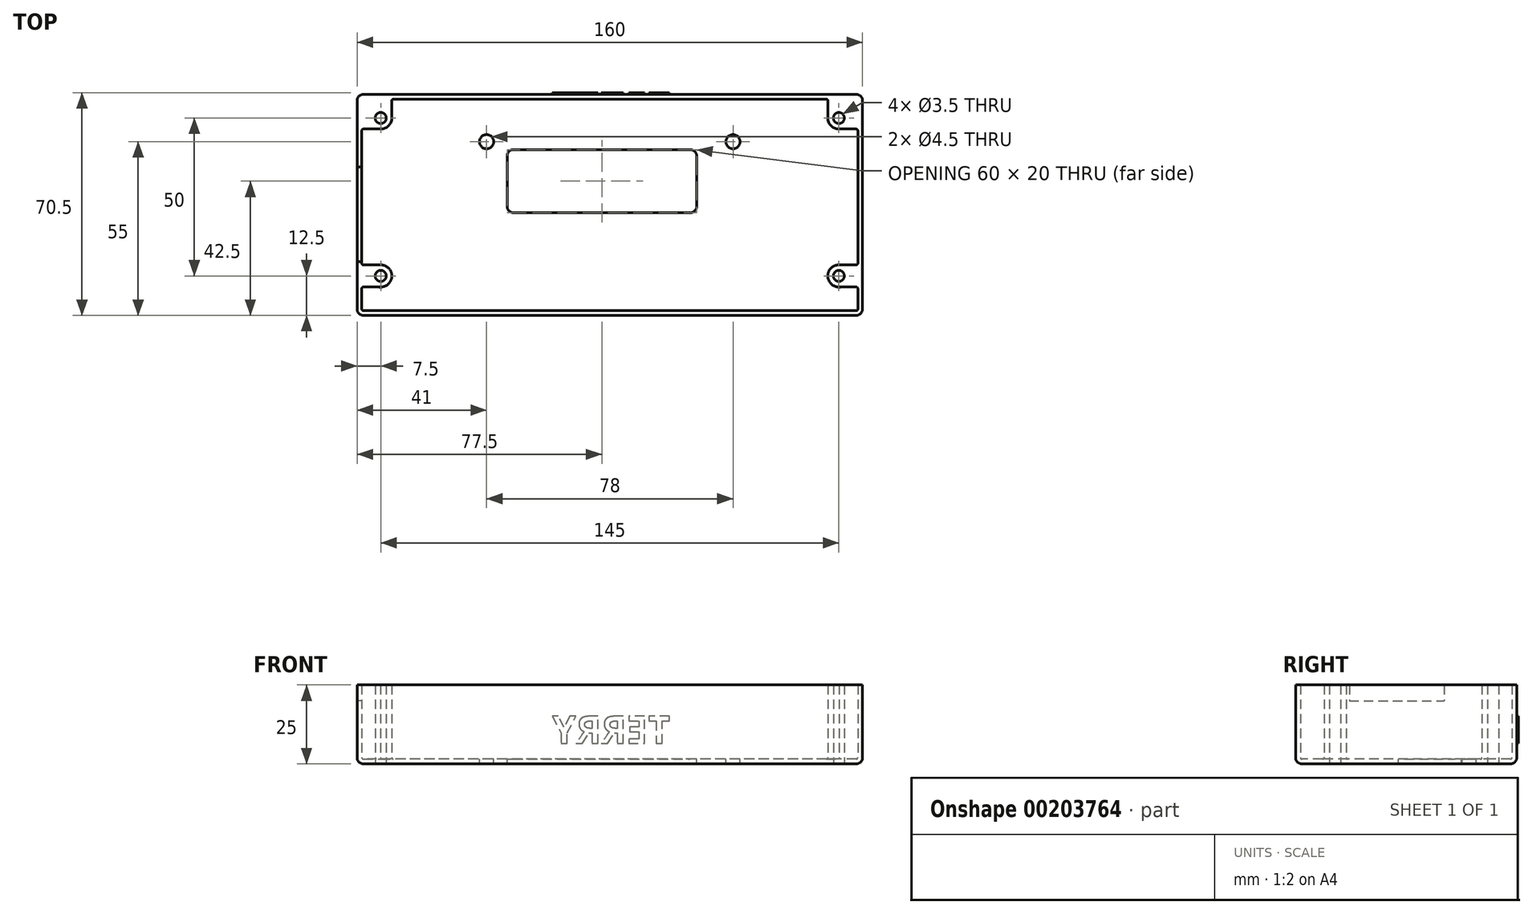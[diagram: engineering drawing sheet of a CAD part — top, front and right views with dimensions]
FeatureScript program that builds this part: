
annotation { "Feature Type Name" : "Feature", "Feature Type Description" : "" }
export const myFeature = defineFeature(function(context is Context, id is Id, definition is map)
    precondition{}
    {
        {
            var Q0;
            Q0=qCreatedBy(makeId("Top.planeOp"),FACE);
            var sketch = newSketch(context, id + "F0", { "sketchPlane" : qUnion([Q0])});
            skLineSegment(sketch, "E0.bottom", {"start": v(80, 35) * mm, "end": v(-80, 35) * mm});
            skLineSegment(sketch, "E0.top", {"start": v(80, -35) * mm, "end": v(-80, -35) * mm});
            skLineSegment(sketch, "E0.left", {"start": v(80, 35) * mm, "end": v(80, -35) * mm});
            skLineSegment(sketch, "E0.right", {"start": v(-80, 35) * mm, "end": v(-80, -35) * mm});
            skPoint(sketch, "E0.middle", {"position": v(0, 0) * mm});
            skLineSegment(sketch, "E1.0", {"start": v(78.5, 33.5) * mm, "end": v(-78.5, 33.5) * mm});
            skLineSegment(sketch, "E2.0", {"start": v(78.5, 33.5) * mm, "end": v(78.5, -33.5) * mm});
            skLineSegment(sketch, "E2.1", {"start": v(78.5, -33.5) * mm, "end": v(-78.5, -33.5) * mm});
            skLineSegment(sketch, "E2.2", {"start": v(-78.5, 33.5) * mm, "end": v(-78.5, -33.5) * mm});
            skSolve(sketch);
        }
        {
            var Q0;
            Q0=makeQuery(id+"F0.imprint","IMPRINT",FACE,{"disambiguationData":[TD([[makeQuery(id+"F0.imprint","IMPRINT",EDGE,{"derivedFrom":sQuery(id+"F0.wireOp",EDGE,"E0.bottom")}),1.0]])]});
            extrude(context, id + "F1", {"entities" : qUnion([Q0]), "depth" : 25 * mm});
        }
        {
            var Q0;
            Q0=qCreatedBy(makeId("Top.planeOp"),FACE);
            var sketch = newSketch(context, id + "F2", { "sketchPlane" : qUnion([Q0])});
            skLineSegment(sketch, "E3.bottom", {"start": v(-80, -35) * mm, "end": v(80, -35) * mm});
            skLineSegment(sketch, "E3.top", {"start": v(-80, 35) * mm, "end": v(80, 35) * mm});
            skLineSegment(sketch, "E3.left", {"start": v(-80, -35) * mm, "end": v(-80, 35) * mm});
            skLineSegment(sketch, "E3.right", {"start": v(80, -35) * mm, "end": v(80, 35) * mm});
            skPoint(sketch, "E3.middle", {"position": v(0, 0) * mm});
            skSolve(sketch);
        }
        {
            var Q0;
            Q0=makeQuery(id+"F2.imprint","IMPRINT",FACE,{"disambiguationData":[TD([[makeQuery(id+"F2.imprint","IMPRINT",EDGE,{"derivedFrom":sQuery(id+"F2.wireOp",EDGE,"E3.bottom")}),1.0]])]});
            extrude(context, id + "F3", {"entities" : qUnion([Q0]), "operationType" : NewBodyOperationType.ADD, "depth" : 1.5 * mm});
        }
        {
            var Q0;
            Q0=qCreatedBy(makeId("Top.planeOp"),FACE);
            var sketch = newSketch(context, id + "F4", { "sketchPlane" : qUnion([Q0])});
            skLineSegment(sketch, "E4", {"start": v(0, 0) * mm, "end": v(0, 27.5) * mm, "construction": true});
            skLineSegment(sketch, "E5", {"start": v(0, 27.5) * mm, "end": v(-72.5, 27.5) * mm, "construction": true});
            skLineSegment(sketch, "E6", {"start": v(-72.5, 27.5) * mm, "end": v(-72.5, -22.5) * mm, "construction": true});
            skLineSegment(sketch, "E7", {"start": v(72.5, -22.5) * mm, "end": v(72.5, 27.5) * mm, "construction": true});
            skArc(sketch, "E8", {"start": v(-72.5, 24) * mm, "mid": v(-70.03, 25.03) * mm, "end": v(-69, 27.5) * mm});
            skArc(sketch, "E9", {"start": v(-72.54, -26) * mm, "mid": v(-69, -22.52) * mm, "end": v(-72.5, -19) * mm});
            skLineSegment(sketch, "E10", {"start": v(0, 27.5) * mm, "end": v(0, 35) * mm, "construction": true});
            skLineSegment(sketch, "E11", {"start": v(0, 35) * mm, "end": v(-80, 35) * mm, "construction": true});
            skLineSegment(sketch, "E12", {"start": v(-80, 35) * mm, "end": v(-80, -35) * mm, "construction": true});
            skLineSegment(sketch, "E13", {"start": v(-69, 27.5) * mm, "end": v(-69, 35) * mm});
            skLineSegment(sketch, "E14", {"start": v(-72.5, 24) * mm, "end": v(-80, 24) * mm});
            skLineSegment(sketch, "E15", {"start": v(-72.5, -19) * mm, "end": v(-80, -19) * mm});
            skLineSegment(sketch, "E16", {"start": v(-72.54, -26) * mm, "end": v(-80, -26) * mm});
            skLineSegment(sketch, "E17.MirrorCS", {"start": v(69, 27.5) * mm, "end": v(69, 35) * mm});
            skArc(sketch, "E18.MirrorCS", {"start": v(72.5, 24) * mm, "mid": v(70.03, 25.03) * mm, "end": v(69, 27.5) * mm});
            skLineSegment(sketch, "E19.MirrorCS", {"start": v(72.5, 24) * mm, "end": v(80, 24) * mm});
            skLineSegment(sketch, "E20.MirrorCS", {"start": v(72.5, -19) * mm, "end": v(80, -19) * mm});
            skArc(sketch, "E21.MirrorCS", {"start": v(72.54, -26) * mm, "mid": v(69, -22.52) * mm, "end": v(72.5, -19) * mm});
            skLineSegment(sketch, "E22.MirrorCS", {"start": v(72.54, -26) * mm, "end": v(80, -26) * mm});
            skLineSegment(sketch, "E23", {"start": v(-80, -19) * mm, "end": v(-80, -26) * mm});
            skLineSegment(sketch, "E24", {"start": v(-80, 24) * mm, "end": v(-80, 35) * mm});
            skLineSegment(sketch, "E25", {"start": v(69, 35) * mm, "end": v(80, 35) * mm});
            skLineSegment(sketch, "E26", {"start": v(80, 24) * mm, "end": v(80, 35) * mm});
            skLineSegment(sketch, "E27", {"start": v(80, -19) * mm, "end": v(80, -26) * mm});
            skLineSegment(sketch, "E28", {"start": v(-80, 35) * mm, "end": v(-69, 35) * mm});
            skCircle(sketch, "E29", {"center": v(-72.5, 27.5) * mm, "radius": 1.75 * mm});
            skCircle(sketch, "E30", {"center": v(72.5, 27.5) * mm, "radius": 1.75 * mm});
            skCircle(sketch, "E31", {"center": v(72.5, -22.5) * mm, "radius": 1.75 * mm});
            skCircle(sketch, "E32", {"center": v(-72.5, -22.5) * mm, "radius": 1.75 * mm});
            skLineSegment(sketch, "E33", {"start": v(-72.5, 27.5) * mm, "end": v(-39, 27.5) * mm, "construction": true});
            skPoint(sketch, "E33.endSnap0", {"position": v(-36.25, 27.5) * mm});
            skLineSegment(sketch, "E34", {"start": v(-39, 27.5) * mm, "end": v(-39, 20) * mm, "construction": true});
            skLineSegment(sketch, "E35", {"start": v(-39, 20) * mm, "end": v(39, 20) * mm, "construction": true});
            skCircle(sketch, "E36", {"center": v(-39, 20) * mm, "radius": 2.25 * mm});
            skCircle(sketch, "E37", {"center": v(39, 20) * mm, "radius": 2.25 * mm});
            skLineSegment(sketch, "E38", {"start": v(-32.5, -2.5) * mm, "end": v(-32.5, 17.5) * mm});
            skLineSegment(sketch, "E39", {"start": v(-32.5, 17.5) * mm, "end": v(27.5, 17.5) * mm});
            skLineSegment(sketch, "E40", {"start": v(27.5, 17.5) * mm, "end": v(27.5, -2.5) * mm});
            skLineSegment(sketch, "E41", {"start": v(27.5, -2.5) * mm, "end": v(-32.5, -2.5) * mm});
            skSolve(sketch);
        }
        {
            var Q0;
            Q0=makeQuery(id+"F4.imprint","IMPRINT",FACE,{"disambiguationData":[TD([[makeQuery(id+"F4.imprint","IMPRINT",EDGE,{"derivedFrom":sQuery(id+"F4.wireOp",EDGE,"E8")}),1.0]])]});
            var Q1;
            Q1=makeQuery(id+"F4.imprint","IMPRINT",FACE,{"disambiguationData":[TD([[makeQuery(id+"F4.imprint","IMPRINT",EDGE,{"derivedFrom":sQuery(id+"F4.wireOp",EDGE,"E9")}),1.0]])]});
            var Q2;
            Q2=makeQuery(id+"F4.imprint","IMPRINT",FACE,{"disambiguationData":[TD([[makeQuery(id+"F4.imprint","IMPRINT",EDGE,{"derivedFrom":sQuery(id+"F4.wireOp",EDGE,"E17.MirrorCS")}),-1.0]])]});
            var Q3;
            Q3=makeQuery(id+"F4.imprint","IMPRINT",FACE,{"disambiguationData":[TD([[makeQuery(id+"F4.imprint","IMPRINT",EDGE,{"derivedFrom":sQuery(id+"F4.wireOp",EDGE,"E20.MirrorCS")}),-1.0]])]});
            var Q4;
            Q4=sQuery(id+"F4.wireOp",EDGE,"E16");
            var Q5;
            Q5=sQuery(id+"F4.wireOp",EDGE,"E15");
            var Q6;
            Q6=sQuery(id+"F4.wireOp",EDGE,"E9");
            var Q7;
            Q7=sQuery(id+"F4.wireOp",EDGE,"E23");
            var Q8;
            Q8=sQuery(id+"F4.wireOp",EDGE,"E21.MirrorCS");
            var Q9;
            Q9=sQuery(id+"F4.wireOp",EDGE,"E27");
            var Q10;
            Q10=sQuery(id+"F4.wireOp",EDGE,"E22.MirrorCS");
            var Q11;
            Q11=sQuery(id+"F4.wireOp",EDGE,"E20.MirrorCS");
            var Q12;
            Q12=sQuery(id+"F4.wireOp",EDGE,"E25");
            var Q13;
            Q13=sQuery(id+"F4.wireOp",EDGE,"E26");
            var Q14;
            Q14=sQuery(id+"F4.wireOp",EDGE,"E19.MirrorCS");
            var Q15;
            Q15=sQuery(id+"F4.wireOp",EDGE,"E17.MirrorCS");
            var Q16;
            Q16=sQuery(id+"F4.wireOp",EDGE,"E18.MirrorCS");
            var Q17;
            Q17=sQuery(id+"F4.wireOp",EDGE,"E14");
            var Q18;
            Q18=sQuery(id+"F4.wireOp",EDGE,"E8");
            var Q19;
            Q19=sQuery(id+"F4.wireOp",EDGE,"E24");
            var Q20;
            Q20=sQuery(id+"F4.wireOp",EDGE,"E13");
            var Q21;
            Q21=sQuery(id+"F4.wireOp",EDGE,"E28");
            extrude(context, id + "F5", {"entities" : qUnion([Q0, Q1, Q2, Q3]), "operationType" : NewBodyOperationType.ADD, "surfaceEntities" : qUnion([Q4, Q5, Q6, Q7, Q8, Q9, Q10, Q11, Q12, Q13, Q14, Q15, Q16, Q17, Q18, Q19, Q20, Q21]), "depth" : 25 * mm});
        }
        {
            var Q0;
            Q0=makeQuery(id+"F5.boolean.opBoolean","SPLIT",FACE,{"disambiguationData":[TD([makeQuery(id+"F5.opExtrude","SWEPT_FACE",FACE,{"disambiguationData":[OSD([sQuery(id+"F4.wireOp",EDGE,"E29")])]})])],"derivedFrom":makeQuery(id+"F3.opExtrude","CAP_FACE",FACE,{"disambiguationData":[OSD([sQuery(id+"F2.wireOp",EDGE,"E3.bottom"),sQuery(id+"F2.wireOp",EDGE,"E3.top"),sQuery(id+"F2.wireOp",EDGE,"E3.left"),sQuery(id+"F2.wireOp",EDGE,"E3.right")])],"isStart":false})});
            var Q1;
            Q1=makeQuery(id+"F5.boolean.opBoolean","SPLIT",FACE,{"disambiguationData":[TD([makeQuery(id+"F5.opExtrude","SWEPT_FACE",FACE,{"disambiguationData":[OSD([sQuery(id+"F4.wireOp",EDGE,"E32")])]})])],"derivedFrom":makeQuery(id+"F3.opExtrude","CAP_FACE",FACE,{"disambiguationData":[OSD([sQuery(id+"F2.wireOp",EDGE,"E3.bottom"),sQuery(id+"F2.wireOp",EDGE,"E3.top"),sQuery(id+"F2.wireOp",EDGE,"E3.left"),sQuery(id+"F2.wireOp",EDGE,"E3.right")])],"isStart":false})});
            var Q2;
            Q2=makeQuery(id+"F5.boolean.opBoolean","SPLIT",FACE,{"disambiguationData":[TD([makeQuery(id+"F5.opExtrude","SWEPT_FACE",FACE,{"disambiguationData":[OSD([sQuery(id+"F4.wireOp",EDGE,"E30")])]})])],"derivedFrom":makeQuery(id+"F3.opExtrude","CAP_FACE",FACE,{"disambiguationData":[OSD([sQuery(id+"F2.wireOp",EDGE,"E3.bottom"),sQuery(id+"F2.wireOp",EDGE,"E3.top"),sQuery(id+"F2.wireOp",EDGE,"E3.left"),sQuery(id+"F2.wireOp",EDGE,"E3.right")])],"isStart":false})});
            var Q3;
            Q3=makeQuery(id+"F5.boolean.opBoolean","SPLIT",FACE,{"disambiguationData":[TD([makeQuery(id+"F5.opExtrude","SWEPT_FACE",FACE,{"disambiguationData":[OSD([sQuery(id+"F4.wireOp",EDGE,"E31")])]})])],"derivedFrom":makeQuery(id+"F3.opExtrude","CAP_FACE",FACE,{"disambiguationData":[OSD([sQuery(id+"F2.wireOp",EDGE,"E3.bottom"),sQuery(id+"F2.wireOp",EDGE,"E3.top"),sQuery(id+"F2.wireOp",EDGE,"E3.left"),sQuery(id+"F2.wireOp",EDGE,"E3.right")])],"isStart":false})});
            extrude(context, id + "F6", {"entities" : qUnion([Q0, Q1, Q2, Q3]), "operationType" : NewBodyOperationType.REMOVE, "endBound" : BoundingType.UP_TO_NEXT, "oppositeDirection" : true, "depth" : 25 * mm});
        }
        {
            var Q0;
            Q0=makeQuery(id+"F5.boolean.opBoolean","SPLIT",FACE,{"disambiguationData":[TD([makeQuery(id+"F1.opExtrude","SWEPT_FACE",FACE,{"disambiguationData":[OSD([sQuery(id+"F0.wireOp",EDGE,"E1.0")])]})])],"derivedFrom":makeQuery(id+"F3.opExtrude","CAP_FACE",FACE,{"disambiguationData":[OSD([sQuery(id+"F2.wireOp",EDGE,"E3.bottom"),sQuery(id+"F2.wireOp",EDGE,"E3.top"),sQuery(id+"F2.wireOp",EDGE,"E3.left"),sQuery(id+"F2.wireOp",EDGE,"E3.right")])],"isStart":false})});
            var sketch = newSketch(context, id + "F7", { "sketchPlane" : qUnion([Q0])});
            skLineSegment(sketch, "E42", {"start": v(-72.5, 27.5) * mm, "end": v(-39, 27.5) * mm, "construction": true});
            skLineSegment(sketch, "E43", {"start": v(-39, 27.5) * mm, "end": v(-39, 20) * mm, "construction": true});
            skLineSegment(sketch, "E44", {"start": v(-39, 20) * mm, "end": v(39, 20) * mm, "construction": true});
            skCircle(sketch, "E45", {"center": v(-39, 20) * mm, "radius": 2.25 * mm});
            skCircle(sketch, "E46", {"center": v(39, 20) * mm, "radius": 2.25 * mm});
            skLineSegment(sketch, "E47.bottom", {"start": v(-32.5, -2.5) * mm, "end": v(27.5, -2.5) * mm});
            skLineSegment(sketch, "E47.top", {"start": v(-32.5, 17.5) * mm, "end": v(27.5, 17.5) * mm});
            skLineSegment(sketch, "E47.left", {"start": v(-32.5, -2.5) * mm, "end": v(-32.5, 17.5) * mm});
            skLineSegment(sketch, "E47.right", {"start": v(27.5, -2.5) * mm, "end": v(27.5, 17.5) * mm});
            skSolve(sketch);
        }
        {
            var Q0;
            Q0=makeQuery(id+"F7.imprint","IMPRINT",FACE,{"disambiguationData":[TD([[makeQuery(id+"F7.imprint","IMPRINT",EDGE,{"derivedFrom":sQuery(id+"F7.wireOp",EDGE,"E47.bottom")}),1.0]])]});
            var Q1;
            Q1=makeQuery(id+"F7.imprint","IMPRINT",FACE,{"disambiguationData":[TD([[makeQuery(id+"F7.imprint","IMPRINT",EDGE,{"derivedFrom":sQuery(id+"F7.wireOp",EDGE,"E45")}),1.0]])]});
            var Q2;
            Q2=makeQuery(id+"F7.imprint","IMPRINT",FACE,{"disambiguationData":[TD([[makeQuery(id+"F7.imprint","IMPRINT",EDGE,{"derivedFrom":sQuery(id+"F7.wireOp",EDGE,"E46")}),1.0]])]});
            extrude(context, id + "F8", {"entities" : qUnion([Q0, Q1, Q2]), "operationType" : NewBodyOperationType.REMOVE, "endBound" : BoundingType.UP_TO_NEXT, "oppositeDirection" : true, "depth" : 25 * mm});
        }
        {
            var Q0;
            Q0=makeQuery(id+"F1.opExtrude","SWEPT_FACE",FACE,{"disambiguationData":[OSD([sQuery(id+"F0.wireOp",EDGE,"E0.right")])]});
            var sketch = newSketch(context, id + "F9", { "sketchPlane" : qUnion([Q0])});
            skLineSegment(sketch, "E48", {"start": v(35, 25) * mm, "end": v(18, 25) * mm});
            skLineSegment(sketch, "E49.bottom", {"start": v(18, 25) * mm, "end": v(-12, 25) * mm});
            skLineSegment(sketch, "E49.top", {"start": v(18, 20) * mm, "end": v(-12, 20) * mm});
            skLineSegment(sketch, "E49.left", {"start": v(18, 25) * mm, "end": v(18, 20) * mm});
            skLineSegment(sketch, "E49.right", {"start": v(-12, 25) * mm, "end": v(-12, 20) * mm});
            skSolve(sketch);
        }
        {
            var Q0;
            Q0=makeQuery(id+"F9.imprint","IMPRINT",FACE,{"disambiguationData":[TD([[makeQuery(id+"F9.imprint","IMPRINT",EDGE,{"derivedFrom":sQuery(id+"F9.wireOp",EDGE,"E49.bottom")}),-1.0]])]});
            extrude(context, id + "F10", {"entities" : qUnion([Q0]), "operationType" : NewBodyOperationType.REMOVE, "endBound" : BoundingType.UP_TO_NEXT, "oppositeDirection" : true, "depth" : 25 * mm});
        }
        {
            var Q0;
            Q0=makeQuery(id+"F3.boolean.opBoolean","INTERSECT",EDGE,{"derivedFrom":[makeQuery(id+"F1.opExtrude","SWEPT_FACE",FACE,{"disambiguationData":[OSD([sQuery(id+"F0.wireOp",EDGE,"E1.0")])]}),makeQuery(id+"F3.opExtrude","CAP_FACE",FACE,{"disambiguationData":[OSD([sQuery(id+"F2.wireOp",EDGE,"E3.bottom"),sQuery(id+"F2.wireOp",EDGE,"E3.top"),sQuery(id+"F2.wireOp",EDGE,"E3.left"),sQuery(id+"F2.wireOp",EDGE,"E3.right")])],"isStart":false})]});
            var Q1;
            Q1=makeQuery(id+"F5.boolean.opBoolean","INTERSECT",EDGE,{"derivedFrom":[makeQuery(id+"F3.opExtrude","CAP_FACE",FACE,{"disambiguationData":[OSD([sQuery(id+"F2.wireOp",EDGE,"E3.bottom"),sQuery(id+"F2.wireOp",EDGE,"E3.top"),sQuery(id+"F2.wireOp",EDGE,"E3.left"),sQuery(id+"F2.wireOp",EDGE,"E3.right")])],"isStart":false}),makeQuery(id+"F5.opExtrude","SWEPT_FACE",FACE,{"disambiguationData":[OSD([sQuery(id+"F4.wireOp",EDGE,"E13")])]})]});
            var Q2;
            Q2=makeQuery(id+"F5.boolean.opBoolean","INTERSECT",EDGE,{"derivedFrom":[makeQuery(id+"F3.opExtrude","CAP_FACE",FACE,{"disambiguationData":[OSD([sQuery(id+"F2.wireOp",EDGE,"E3.bottom"),sQuery(id+"F2.wireOp",EDGE,"E3.top"),sQuery(id+"F2.wireOp",EDGE,"E3.left"),sQuery(id+"F2.wireOp",EDGE,"E3.right")])],"isStart":false}),makeQuery(id+"F5.opExtrude","SWEPT_FACE",FACE,{"disambiguationData":[OSD([sQuery(id+"F4.wireOp",EDGE,"E8")])]})]});
            var Q3;
            Q3=makeQuery(id+"F5.boolean.opBoolean","INTERSECT",EDGE,{"derivedFrom":[makeQuery(id+"F3.opExtrude","CAP_FACE",FACE,{"disambiguationData":[OSD([sQuery(id+"F2.wireOp",EDGE,"E3.bottom"),sQuery(id+"F2.wireOp",EDGE,"E3.top"),sQuery(id+"F2.wireOp",EDGE,"E3.left"),sQuery(id+"F2.wireOp",EDGE,"E3.right")])],"isStart":false}),makeQuery(id+"F5.opExtrude","SWEPT_FACE",FACE,{"disambiguationData":[OSD([sQuery(id+"F4.wireOp",EDGE,"E14")])]})]});
            var Q4;
            {var subQ0=makeQuery(id+"F1.opExtrude","SWEPT_FACE",FACE,{"disambiguationData":[OSD([sQuery(id+"F0.wireOp",EDGE,"E2.2")])]});var subQ1=makeQuery(id+"F3.opExtrude","CAP_FACE",FACE,{"disambiguationData":[OSD([sQuery(id+"F2.wireOp",EDGE,"E3.bottom"),sQuery(id+"F2.wireOp",EDGE,"E3.top"),sQuery(id+"F2.wireOp",EDGE,"E3.left"),sQuery(id+"F2.wireOp",EDGE,"E3.right")])],"isStart":false});Q4=makeQuery(id+"F5.boolean.opBoolean","SPLIT",EDGE,{"disambiguationData":[TD([makeQuery(id+"F5.opExtrude","SWEPT_FACE",FACE,{"disambiguationData":[OSD([sQuery(id+"F4.wireOp",EDGE,"E14")])]})])],"derivedFrom":makeQuery(id+"F3.boolean.opBoolean","INTERSECT",EDGE,{"derivedFrom":[subQ0,subQ1]})});}
            var Q5;
            Q5=makeQuery(id+"F5.boolean.opBoolean","INTERSECT",EDGE,{"derivedFrom":[makeQuery(id+"F3.opExtrude","CAP_FACE",FACE,{"disambiguationData":[OSD([sQuery(id+"F2.wireOp",EDGE,"E3.bottom"),sQuery(id+"F2.wireOp",EDGE,"E3.top"),sQuery(id+"F2.wireOp",EDGE,"E3.left"),sQuery(id+"F2.wireOp",EDGE,"E3.right")])],"isStart":false}),makeQuery(id+"F5.opExtrude","SWEPT_FACE",FACE,{"disambiguationData":[OSD([sQuery(id+"F4.wireOp",EDGE,"E9")])]})]});
            var Q6;
            Q6=makeQuery(id+"F5.boolean.opBoolean","INTERSECT",EDGE,{"derivedFrom":[makeQuery(id+"F3.opExtrude","CAP_FACE",FACE,{"disambiguationData":[OSD([sQuery(id+"F2.wireOp",EDGE,"E3.bottom"),sQuery(id+"F2.wireOp",EDGE,"E3.top"),sQuery(id+"F2.wireOp",EDGE,"E3.left"),sQuery(id+"F2.wireOp",EDGE,"E3.right")])],"isStart":false}),makeQuery(id+"F5.opExtrude","SWEPT_FACE",FACE,{"disambiguationData":[OSD([sQuery(id+"F4.wireOp",EDGE,"E16")])]})]});
            var Q7;
            {var subQ0=makeQuery(id+"F1.opExtrude","SWEPT_FACE",FACE,{"disambiguationData":[OSD([sQuery(id+"F0.wireOp",EDGE,"E2.2")])]});var subQ1=makeQuery(id+"F3.opExtrude","CAP_FACE",FACE,{"disambiguationData":[OSD([sQuery(id+"F2.wireOp",EDGE,"E3.bottom"),sQuery(id+"F2.wireOp",EDGE,"E3.top"),sQuery(id+"F2.wireOp",EDGE,"E3.left"),sQuery(id+"F2.wireOp",EDGE,"E3.right")])],"isStart":false});Q7=makeQuery(id+"F5.boolean.opBoolean","SPLIT",EDGE,{"disambiguationData":[TD([makeQuery(id+"F1.opExtrude","SWEPT_FACE",FACE,{"disambiguationData":[OSD([sQuery(id+"F0.wireOp",EDGE,"E2.1")])]})])],"derivedFrom":makeQuery(id+"F3.boolean.opBoolean","INTERSECT",EDGE,{"derivedFrom":[subQ0,subQ1]})});}
            var Q8;
            Q8=makeQuery(id+"F5.boolean.opBoolean","INTERSECT",EDGE,{"derivedFrom":[makeQuery(id+"F1.opExtrude","SWEPT_FACE",FACE,{"disambiguationData":[OSD([sQuery(id+"F0.wireOp",EDGE,"E2.2")])]}),makeQuery(id+"F5.opExtrude","SWEPT_FACE",FACE,{"disambiguationData":[OSD([sQuery(id+"F4.wireOp",EDGE,"E14")])]})]});
            var Q9;
            Q9=makeQuery(id+"F5.boolean.opBoolean","INTERSECT",EDGE,{"derivedFrom":[makeQuery(id+"F1.opExtrude","SWEPT_FACE",FACE,{"disambiguationData":[OSD([sQuery(id+"F0.wireOp",EDGE,"E1.0")])]}),makeQuery(id+"F5.opExtrude","SWEPT_FACE",FACE,{"disambiguationData":[OSD([sQuery(id+"F4.wireOp",EDGE,"E13")])]})]});
            var Q10;
            Q10=makeQuery(id+"F5.boolean.opBoolean","INTERSECT",EDGE,{"derivedFrom":[makeQuery(id+"F1.opExtrude","SWEPT_FACE",FACE,{"disambiguationData":[OSD([sQuery(id+"F0.wireOp",EDGE,"E2.2")])]}),makeQuery(id+"F5.opExtrude","SWEPT_FACE",FACE,{"disambiguationData":[OSD([sQuery(id+"F4.wireOp",EDGE,"E16")])]})]});
            var Q11;
            Q11=makeQuery(id+"F3.boolean.opBoolean","INTERSECT",EDGE,{"derivedFrom":[makeQuery(id+"F1.opExtrude","SWEPT_FACE",FACE,{"disambiguationData":[OSD([sQuery(id+"F0.wireOp",EDGE,"E2.1")])]}),makeQuery(id+"F3.opExtrude","CAP_FACE",FACE,{"disambiguationData":[OSD([sQuery(id+"F2.wireOp",EDGE,"E3.bottom"),sQuery(id+"F2.wireOp",EDGE,"E3.top"),sQuery(id+"F2.wireOp",EDGE,"E3.left"),sQuery(id+"F2.wireOp",EDGE,"E3.right")])],"isStart":false})]});
            var Q12;
            Q12=makeQuery(id+"F5.boolean.opBoolean","INTERSECT",EDGE,{"derivedFrom":[makeQuery(id+"F3.opExtrude","CAP_FACE",FACE,{"disambiguationData":[OSD([sQuery(id+"F2.wireOp",EDGE,"E3.bottom"),sQuery(id+"F2.wireOp",EDGE,"E3.top"),sQuery(id+"F2.wireOp",EDGE,"E3.left"),sQuery(id+"F2.wireOp",EDGE,"E3.right")])],"isStart":false}),makeQuery(id+"F5.opExtrude","SWEPT_FACE",FACE,{"disambiguationData":[OSD([sQuery(id+"F4.wireOp",EDGE,"E15")])]})]});
            var Q13;
            {var subQ0=makeQuery(id+"F1.opExtrude","SWEPT_FACE",FACE,{"disambiguationData":[OSD([sQuery(id+"F0.wireOp",EDGE,"E2.0")])]});var subQ1=makeQuery(id+"F3.opExtrude","CAP_FACE",FACE,{"disambiguationData":[OSD([sQuery(id+"F2.wireOp",EDGE,"E3.bottom"),sQuery(id+"F2.wireOp",EDGE,"E3.top"),sQuery(id+"F2.wireOp",EDGE,"E3.left"),sQuery(id+"F2.wireOp",EDGE,"E3.right")])],"isStart":false});Q13=makeQuery(id+"F5.boolean.opBoolean","SPLIT",EDGE,{"disambiguationData":[TD([makeQuery(id+"F5.opExtrude","SWEPT_FACE",FACE,{"disambiguationData":[OSD([sQuery(id+"F4.wireOp",EDGE,"E19.MirrorCS")])]})])],"derivedFrom":makeQuery(id+"F3.boolean.opBoolean","INTERSECT",EDGE,{"derivedFrom":[subQ0,subQ1]})});}
            var Q14;
            Q14=makeQuery(id+"F5.boolean.opBoolean","INTERSECT",EDGE,{"derivedFrom":[makeQuery(id+"F3.opExtrude","CAP_FACE",FACE,{"disambiguationData":[OSD([sQuery(id+"F2.wireOp",EDGE,"E3.bottom"),sQuery(id+"F2.wireOp",EDGE,"E3.top"),sQuery(id+"F2.wireOp",EDGE,"E3.left"),sQuery(id+"F2.wireOp",EDGE,"E3.right")])],"isStart":false}),makeQuery(id+"F5.opExtrude","SWEPT_FACE",FACE,{"disambiguationData":[OSD([sQuery(id+"F4.wireOp",EDGE,"E19.MirrorCS")])]})]});
            var Q15;
            Q15=makeQuery(id+"F5.boolean.opBoolean","INTERSECT",EDGE,{"derivedFrom":[makeQuery(id+"F3.opExtrude","CAP_FACE",FACE,{"disambiguationData":[OSD([sQuery(id+"F2.wireOp",EDGE,"E3.bottom"),sQuery(id+"F2.wireOp",EDGE,"E3.top"),sQuery(id+"F2.wireOp",EDGE,"E3.left"),sQuery(id+"F2.wireOp",EDGE,"E3.right")])],"isStart":false}),makeQuery(id+"F5.opExtrude","SWEPT_FACE",FACE,{"disambiguationData":[OSD([sQuery(id+"F4.wireOp",EDGE,"E18.MirrorCS")])]})]});
            var Q16;
            Q16=makeQuery(id+"F5.boolean.opBoolean","INTERSECT",EDGE,{"derivedFrom":[makeQuery(id+"F3.opExtrude","CAP_FACE",FACE,{"disambiguationData":[OSD([sQuery(id+"F2.wireOp",EDGE,"E3.bottom"),sQuery(id+"F2.wireOp",EDGE,"E3.top"),sQuery(id+"F2.wireOp",EDGE,"E3.left"),sQuery(id+"F2.wireOp",EDGE,"E3.right")])],"isStart":false}),makeQuery(id+"F5.opExtrude","SWEPT_FACE",FACE,{"disambiguationData":[OSD([sQuery(id+"F4.wireOp",EDGE,"E17.MirrorCS")])]})]});
            var Q17;
            Q17=makeQuery(id+"F5.boolean.opBoolean","INTERSECT",EDGE,{"derivedFrom":[makeQuery(id+"F3.opExtrude","CAP_FACE",FACE,{"disambiguationData":[OSD([sQuery(id+"F2.wireOp",EDGE,"E3.bottom"),sQuery(id+"F2.wireOp",EDGE,"E3.top"),sQuery(id+"F2.wireOp",EDGE,"E3.left"),sQuery(id+"F2.wireOp",EDGE,"E3.right")])],"isStart":false}),makeQuery(id+"F5.opExtrude","SWEPT_FACE",FACE,{"disambiguationData":[OSD([sQuery(id+"F4.wireOp",EDGE,"E21.MirrorCS")])]})]});
            var Q18;
            Q18=makeQuery(id+"F5.boolean.opBoolean","INTERSECT",EDGE,{"derivedFrom":[makeQuery(id+"F3.opExtrude","CAP_FACE",FACE,{"disambiguationData":[OSD([sQuery(id+"F2.wireOp",EDGE,"E3.bottom"),sQuery(id+"F2.wireOp",EDGE,"E3.top"),sQuery(id+"F2.wireOp",EDGE,"E3.left"),sQuery(id+"F2.wireOp",EDGE,"E3.right")])],"isStart":false}),makeQuery(id+"F5.opExtrude","SWEPT_FACE",FACE,{"disambiguationData":[OSD([sQuery(id+"F4.wireOp",EDGE,"E22.MirrorCS")])]})]});
            var Q19;
            {var subQ0=makeQuery(id+"F1.opExtrude","SWEPT_FACE",FACE,{"disambiguationData":[OSD([sQuery(id+"F0.wireOp",EDGE,"E2.0")])]});var subQ1=makeQuery(id+"F3.opExtrude","CAP_FACE",FACE,{"disambiguationData":[OSD([sQuery(id+"F2.wireOp",EDGE,"E3.bottom"),sQuery(id+"F2.wireOp",EDGE,"E3.top"),sQuery(id+"F2.wireOp",EDGE,"E3.left"),sQuery(id+"F2.wireOp",EDGE,"E3.right")])],"isStart":false});Q19=makeQuery(id+"F5.boolean.opBoolean","SPLIT",EDGE,{"disambiguationData":[TD([makeQuery(id+"F1.opExtrude","SWEPT_FACE",FACE,{"disambiguationData":[OSD([sQuery(id+"F0.wireOp",EDGE,"E2.1")])]})])],"derivedFrom":makeQuery(id+"F3.boolean.opBoolean","INTERSECT",EDGE,{"derivedFrom":[subQ0,subQ1]})});}
            var Q20;
            Q20=makeQuery(id+"F5.boolean.opBoolean","INTERSECT",EDGE,{"derivedFrom":[makeQuery(id+"F1.opExtrude","SWEPT_FACE",FACE,{"disambiguationData":[OSD([sQuery(id+"F0.wireOp",EDGE,"E1.0")])]}),makeQuery(id+"F5.opExtrude","SWEPT_FACE",FACE,{"disambiguationData":[OSD([sQuery(id+"F4.wireOp",EDGE,"E17.MirrorCS")])]})]});
            var Q21;
            Q21=makeQuery(id+"F5.boolean.opBoolean","INTERSECT",EDGE,{"derivedFrom":[makeQuery(id+"F1.opExtrude","SWEPT_FACE",FACE,{"disambiguationData":[OSD([sQuery(id+"F0.wireOp",EDGE,"E2.0")])]}),makeQuery(id+"F5.opExtrude","SWEPT_FACE",FACE,{"disambiguationData":[OSD([sQuery(id+"F4.wireOp",EDGE,"E19.MirrorCS")])]})]});
            var Q22;
            Q22=makeQuery(id+"F5.boolean.opBoolean","INTERSECT",EDGE,{"derivedFrom":[makeQuery(id+"F1.opExtrude","SWEPT_FACE",FACE,{"disambiguationData":[OSD([sQuery(id+"F0.wireOp",EDGE,"E2.0")])]}),makeQuery(id+"F5.opExtrude","SWEPT_FACE",FACE,{"disambiguationData":[OSD([sQuery(id+"F4.wireOp",EDGE,"E22.MirrorCS")])]})]});
            var Q23;
            Q23=makeQuery(id+"F1.opExtrude","SWEPT_EDGE",EDGE,{"disambiguationData":[OSD([sQuery(id+"F0.wireOp",EDGE,"E2.0"),sQuery(id+"F0.wireOp",EDGE,"E2.1")])]});
            var Q24;
            Q24=makeQuery(id+"F5.boolean.opBoolean","INTERSECT",EDGE,{"derivedFrom":[makeQuery(id+"F3.opExtrude","CAP_FACE",FACE,{"disambiguationData":[OSD([sQuery(id+"F2.wireOp",EDGE,"E3.bottom"),sQuery(id+"F2.wireOp",EDGE,"E3.top"),sQuery(id+"F2.wireOp",EDGE,"E3.left"),sQuery(id+"F2.wireOp",EDGE,"E3.right")])],"isStart":false}),makeQuery(id+"F5.opExtrude","SWEPT_FACE",FACE,{"disambiguationData":[OSD([sQuery(id+"F4.wireOp",EDGE,"E20.MirrorCS")])]})]});
            var Q25;
            Q25=makeQuery(id+"F5.boolean.opBoolean","INTERSECT",EDGE,{"derivedFrom":[makeQuery(id+"F1.opExtrude","SWEPT_FACE",FACE,{"disambiguationData":[OSD([sQuery(id+"F0.wireOp",EDGE,"E2.2")])]}),makeQuery(id+"F5.opExtrude","SWEPT_FACE",FACE,{"disambiguationData":[OSD([sQuery(id+"F4.wireOp",EDGE,"E15")])]})]});
            var Q26;
            Q26=makeQuery(id+"F1.opExtrude","SWEPT_EDGE",EDGE,{"disambiguationData":[OSD([sQuery(id+"F0.wireOp",EDGE,"E2.1"),sQuery(id+"F0.wireOp",EDGE,"E2.2")])]});
            var Q27;
            Q27=makeQuery(id+"F5.boolean.opBoolean","INTERSECT",EDGE,{"derivedFrom":[makeQuery(id+"F1.opExtrude","SWEPT_FACE",FACE,{"disambiguationData":[OSD([sQuery(id+"F0.wireOp",EDGE,"E2.0")])]}),makeQuery(id+"F5.opExtrude","SWEPT_FACE",FACE,{"disambiguationData":[OSD([sQuery(id+"F4.wireOp",EDGE,"E20.MirrorCS")])]})]});
            var Q28;
            Q28=makeQuery(id+"F8.boolean.opBoolean","COPY",EDGE,{"derivedFrom":makeQuery(id+"F8.opExtrude","CAP_EDGE",EDGE,{"disambiguationData":[OSD([sQuery(id+"F7.wireOp",EDGE,"E47.top")])],"isStart":true})});
            var Q29;
            Q29=makeQuery(id+"F8.boolean.opBoolean","COPY",EDGE,{"derivedFrom":makeQuery(id+"F8.opExtrude","TWEAK_EDGE",EDGE,{"derivedFrom":[makeQuery(id+"F3.boolean.opBoolean","MERGE",FACE,{"derivedFrom":[makeQuery(id+"F1.opExtrude","CAP_FACE",FACE,{"disambiguationData":[OSD([sQuery(id+"F0.wireOp",EDGE,"E0.bottom"),sQuery(id+"F0.wireOp",EDGE,"E0.top"),sQuery(id+"F0.wireOp",EDGE,"E0.left"),sQuery(id+"F0.wireOp",EDGE,"E0.right"),sQuery(id+"F0.wireOp",EDGE,"E1.0"),sQuery(id+"F0.wireOp",EDGE,"E2.0"),sQuery(id+"F0.wireOp",EDGE,"E2.1"),sQuery(id+"F0.wireOp",EDGE,"E2.2")])],"isStart":true}),makeQuery(id+"F3.opExtrude","CAP_FACE",FACE,{"disambiguationData":[OSD([sQuery(id+"F2.wireOp",EDGE,"E3.bottom"),sQuery(id+"F2.wireOp",EDGE,"E3.top"),sQuery(id+"F2.wireOp",EDGE,"E3.left"),sQuery(id+"F2.wireOp",EDGE,"E3.right")])],"isStart":true})]}),makeQuery(id+"F7.imprint","IMPRINT",EDGE,{"derivedFrom":sQuery(id+"F7.wireOp",EDGE,"E47.top")})]})});
            var Q30;
            Q30=makeQuery(id+"F8.boolean.opBoolean","COPY",EDGE,{"derivedFrom":makeQuery(id+"F8.opExtrude","CAP_EDGE",EDGE,{"disambiguationData":[OSD([sQuery(id+"F7.wireOp",EDGE,"E47.right")])],"isStart":true})});
            var Q31;
            Q31=makeQuery(id+"F8.boolean.opBoolean","COPY",EDGE,{"derivedFrom":makeQuery(id+"F8.opExtrude","CAP_EDGE",EDGE,{"disambiguationData":[OSD([sQuery(id+"F7.wireOp",EDGE,"E47.bottom")])],"isStart":true})});
            var Q32;
            Q32=makeQuery(id+"F8.boolean.opBoolean","COPY",EDGE,{"derivedFrom":makeQuery(id+"F8.opExtrude","CAP_EDGE",EDGE,{"disambiguationData":[OSD([sQuery(id+"F7.wireOp",EDGE,"E47.left")])],"isStart":true})});
            var Q33;
            Q33=makeQuery(id+"F8.boolean.opBoolean","COPY",EDGE,{"derivedFrom":makeQuery(id+"F8.opExtrude","TWEAK_EDGE",EDGE,{"derivedFrom":[makeQuery(id+"F3.boolean.opBoolean","MERGE",FACE,{"derivedFrom":[makeQuery(id+"F1.opExtrude","CAP_FACE",FACE,{"disambiguationData":[OSD([sQuery(id+"F0.wireOp",EDGE,"E0.bottom"),sQuery(id+"F0.wireOp",EDGE,"E0.top"),sQuery(id+"F0.wireOp",EDGE,"E0.left"),sQuery(id+"F0.wireOp",EDGE,"E0.right"),sQuery(id+"F0.wireOp",EDGE,"E1.0"),sQuery(id+"F0.wireOp",EDGE,"E2.0"),sQuery(id+"F0.wireOp",EDGE,"E2.1"),sQuery(id+"F0.wireOp",EDGE,"E2.2")])],"isStart":true}),makeQuery(id+"F3.opExtrude","CAP_FACE",FACE,{"disambiguationData":[OSD([sQuery(id+"F2.wireOp",EDGE,"E3.bottom"),sQuery(id+"F2.wireOp",EDGE,"E3.top"),sQuery(id+"F2.wireOp",EDGE,"E3.left"),sQuery(id+"F2.wireOp",EDGE,"E3.right")])],"isStart":true})]}),makeQuery(id+"F7.imprint","IMPRINT",EDGE,{"derivedFrom":sQuery(id+"F7.wireOp",EDGE,"E47.right")})]})});
            var Q34;
            Q34=makeQuery(id+"F8.boolean.opBoolean","COPY",EDGE,{"derivedFrom":makeQuery(id+"F8.opExtrude","TWEAK_EDGE",EDGE,{"derivedFrom":[makeQuery(id+"F3.boolean.opBoolean","MERGE",FACE,{"derivedFrom":[makeQuery(id+"F1.opExtrude","CAP_FACE",FACE,{"disambiguationData":[OSD([sQuery(id+"F0.wireOp",EDGE,"E0.bottom"),sQuery(id+"F0.wireOp",EDGE,"E0.top"),sQuery(id+"F0.wireOp",EDGE,"E0.left"),sQuery(id+"F0.wireOp",EDGE,"E0.right"),sQuery(id+"F0.wireOp",EDGE,"E1.0"),sQuery(id+"F0.wireOp",EDGE,"E2.0"),sQuery(id+"F0.wireOp",EDGE,"E2.1"),sQuery(id+"F0.wireOp",EDGE,"E2.2")])],"isStart":true}),makeQuery(id+"F3.opExtrude","CAP_FACE",FACE,{"disambiguationData":[OSD([sQuery(id+"F2.wireOp",EDGE,"E3.bottom"),sQuery(id+"F2.wireOp",EDGE,"E3.top"),sQuery(id+"F2.wireOp",EDGE,"E3.left"),sQuery(id+"F2.wireOp",EDGE,"E3.right")])],"isStart":true})]}),makeQuery(id+"F7.imprint","IMPRINT",EDGE,{"derivedFrom":sQuery(id+"F7.wireOp",EDGE,"E47.bottom")})]})});
            var Q35;
            Q35=makeQuery(id+"F8.boolean.opBoolean","COPY",EDGE,{"derivedFrom":makeQuery(id+"F8.opExtrude","TWEAK_EDGE",EDGE,{"derivedFrom":[makeQuery(id+"F3.boolean.opBoolean","MERGE",FACE,{"derivedFrom":[makeQuery(id+"F1.opExtrude","CAP_FACE",FACE,{"disambiguationData":[OSD([sQuery(id+"F0.wireOp",EDGE,"E0.bottom"),sQuery(id+"F0.wireOp",EDGE,"E0.top"),sQuery(id+"F0.wireOp",EDGE,"E0.left"),sQuery(id+"F0.wireOp",EDGE,"E0.right"),sQuery(id+"F0.wireOp",EDGE,"E1.0"),sQuery(id+"F0.wireOp",EDGE,"E2.0"),sQuery(id+"F0.wireOp",EDGE,"E2.1"),sQuery(id+"F0.wireOp",EDGE,"E2.2")])],"isStart":true}),makeQuery(id+"F3.opExtrude","CAP_FACE",FACE,{"disambiguationData":[OSD([sQuery(id+"F2.wireOp",EDGE,"E3.bottom"),sQuery(id+"F2.wireOp",EDGE,"E3.top"),sQuery(id+"F2.wireOp",EDGE,"E3.left"),sQuery(id+"F2.wireOp",EDGE,"E3.right")])],"isStart":true})]}),makeQuery(id+"F7.imprint","IMPRINT",EDGE,{"derivedFrom":sQuery(id+"F7.wireOp",EDGE,"E47.left")})]})});
            fillet(context, id + "F11", {"entities" : qUnion([Q0, Q1, Q2, Q3, Q4, Q5, Q6, Q7, Q8, Q9, Q10, Q11, Q12, Q13, Q14, Q15, Q16, Q17, Q18, Q19, Q20, Q21, Q22, Q23, Q24, Q25, Q26, Q27, Q28, Q29, Q30, Q31, Q32, Q33, Q34, Q35]), "radius" : 0.5 * mm, "tangentPropagation" : true, "allowEdgeOverflow" : false});
        }
        {
            var Q0;
            Q0=makeQuery(id+"F1.opExtrude","SWEPT_EDGE",EDGE,{"disambiguationData":[OSD([sQuery(id+"F0.wireOp",EDGE,"E0.bottom"),sQuery(id+"F0.wireOp",EDGE,"E0.right")])]});
            var Q1;
            Q1=makeQuery(id+"F1.opExtrude","SWEPT_EDGE",EDGE,{"disambiguationData":[OSD([sQuery(id+"F0.wireOp",EDGE,"E0.top"),sQuery(id+"F0.wireOp",EDGE,"E0.right")])]});
            var Q2;
            Q2=makeQuery(id+"F1.opExtrude","SWEPT_EDGE",EDGE,{"disambiguationData":[OSD([sQuery(id+"F0.wireOp",EDGE,"E0.top"),sQuery(id+"F0.wireOp",EDGE,"E0.left")])]});
            var Q3;
            Q3=makeQuery(id+"F1.opExtrude","SWEPT_EDGE",EDGE,{"disambiguationData":[OSD([sQuery(id+"F0.wireOp",EDGE,"E0.bottom"),sQuery(id+"F0.wireOp",EDGE,"E0.left")])]});
            var Q4;
            Q4=makeQuery(id+"F8.boolean.opBoolean","COPY",EDGE,{"derivedFrom":makeQuery(id+"F8.opExtrude","SWEPT_EDGE",EDGE,{"disambiguationData":[OSD([sQuery(id+"F7.wireOp",EDGE,"E47.bottom"),sQuery(id+"F7.wireOp",EDGE,"E47.left")])]})});
            var Q5;
            Q5=makeQuery(id+"F8.boolean.opBoolean","COPY",EDGE,{"derivedFrom":makeQuery(id+"F8.opExtrude","SWEPT_EDGE",EDGE,{"disambiguationData":[OSD([sQuery(id+"F7.wireOp",EDGE,"E47.top"),sQuery(id+"F7.wireOp",EDGE,"E47.left")])]})});
            var Q6;
            Q6=makeQuery(id+"F8.boolean.opBoolean","COPY",EDGE,{"derivedFrom":makeQuery(id+"F8.opExtrude","SWEPT_EDGE",EDGE,{"disambiguationData":[OSD([sQuery(id+"F7.wireOp",EDGE,"E47.top"),sQuery(id+"F7.wireOp",EDGE,"E47.right")])]})});
            var Q7;
            Q7=makeQuery(id+"F8.boolean.opBoolean","COPY",EDGE,{"derivedFrom":makeQuery(id+"F8.opExtrude","SWEPT_EDGE",EDGE,{"disambiguationData":[OSD([sQuery(id+"F7.wireOp",EDGE,"E47.bottom"),sQuery(id+"F7.wireOp",EDGE,"E47.right")])]})});
            var Q8;
            Q8=makeQuery(id+"F1.opExtrude","CAP_EDGE",EDGE,{"disambiguationData":[OSD([sQuery(id+"F0.wireOp",EDGE,"E0.bottom")])],"isStart":true});
            var Q9;
            Q9=makeQuery(id+"F1.opExtrude","CAP_EDGE",EDGE,{"disambiguationData":[OSD([sQuery(id+"F0.wireOp",EDGE,"E0.right")])],"isStart":true});
            var Q10;
            Q10=makeQuery(id+"F1.opExtrude","CAP_EDGE",EDGE,{"disambiguationData":[OSD([sQuery(id+"F0.wireOp",EDGE,"E0.left")])],"isStart":true});
            var Q11;
            Q11=makeQuery(id+"F1.opExtrude","CAP_EDGE",EDGE,{"disambiguationData":[OSD([sQuery(id+"F0.wireOp",EDGE,"E0.top")])],"isStart":true});
            fillet(context, id + "F12", {"entities" : qUnion([Q0, Q1, Q2, Q3, Q4, Q5, Q6, Q7, Q8, Q9, Q10, Q11]), "radius" : 2 * mm, "tangentPropagation" : true, "allowEdgeOverflow" : false});
        }
        {
            var Q0;
            Q0=makeQuery(id+"F1.opExtrude","SWEPT_FACE",FACE,{"disambiguationData":[OSD([sQuery(id+"F0.wireOp",EDGE,"E0.bottom")])]});
            var sketch = newSketch(context, id + "F13", { "sketchPlane" : qUnion([Q0])});
            skText(sketch, "E50", { "text": "TERRY", "fontName": "OpenSans-Bold.ttf"});
            const initialGuessF13  = {"E50": [-0.01912, 0.00644, 1, 0, 0.00873]};
            skSetInitialGuess(sketch, initialGuessF13);
            skSolve(sketch);
        }
        {
            var Q0;
            Q0 = qSketchRegion(id + "F13", true);
            extrude(context, id + "F14", {"entities" : qUnion([Q0]), "operationType" : NewBodyOperationType.ADD, "depth" : 0.5 * mm});
        }
    });
